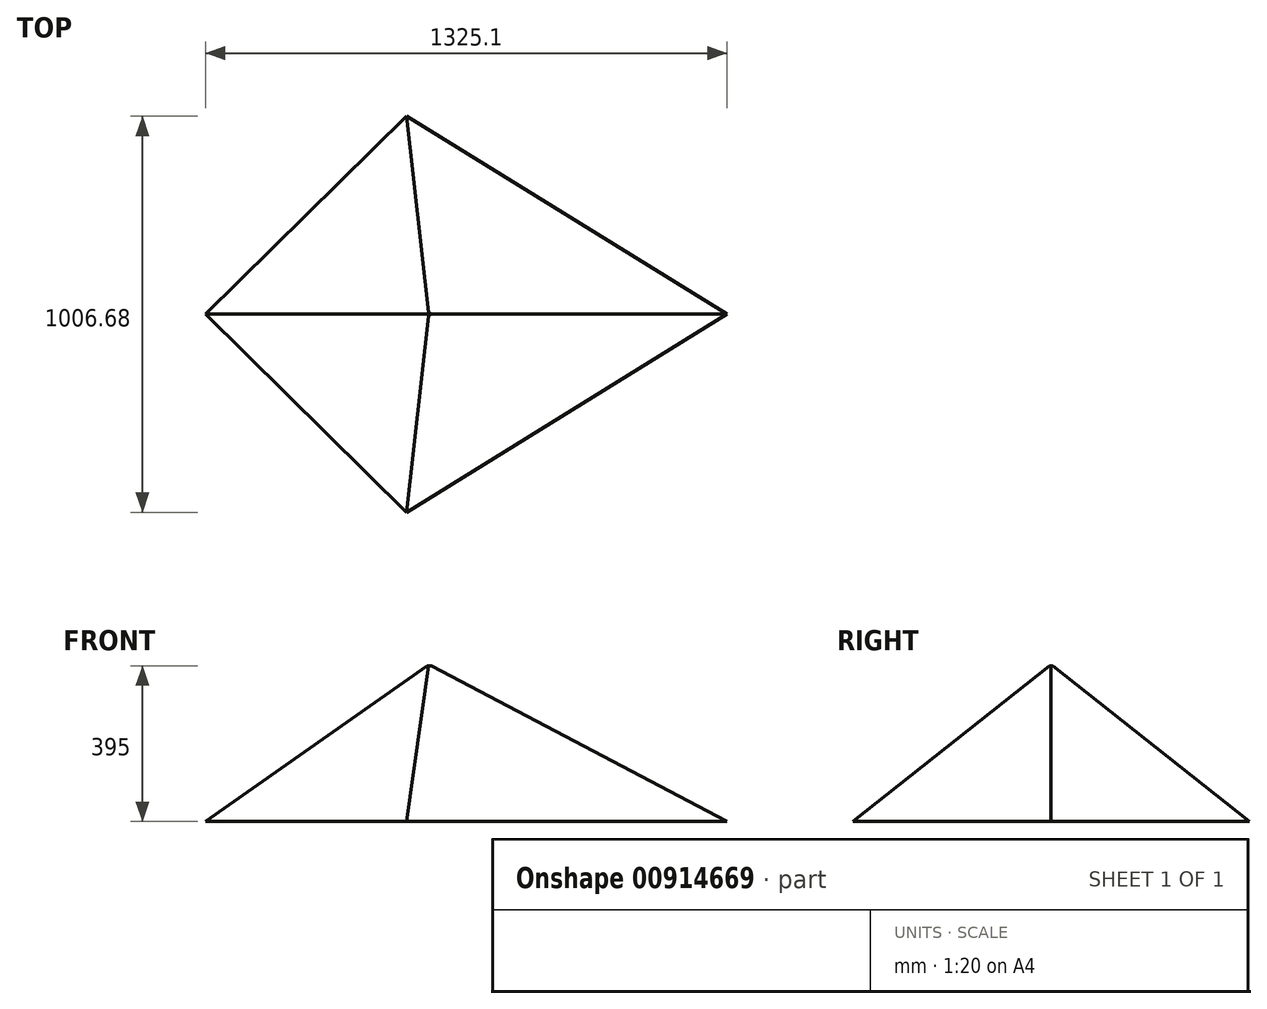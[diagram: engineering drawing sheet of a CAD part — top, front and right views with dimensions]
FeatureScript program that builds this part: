
annotation { "Feature Type Name" : "Feature", "Feature Type Description" : "" }
export const myFeature = defineFeature(function(context is Context, id is Id, definition is map)
    precondition{}
    {
        {
            var Q0;
            Q0=qCreatedBy(makeId("Top.planeOp"),FACE);
            var sketch = newSketch(context, id + "F0", { "sketchPlane" : qUnion([Q0])});
            skLineSegment(sketch, "E0", {"start": v(-534.54, 0) * mm, "end": v(0, -526.09) * mm});
            skLineSegment(sketch, "E1", {"start": v(0, -526.09) * mm, "end": v(850.43, 0) * mm});
            skLineSegment(sketch, "E2", {"start": v(850.43, 0) * mm, "end": v(0, 526.09) * mm});
            skLineSegment(sketch, "E3", {"start": v(0, 526.09) * mm, "end": v(-534.54, 0) * mm});
            skLineSegment(sketch, "E4.0", {"start": v(2.55, 503.34) * mm, "end": v(-508.88, 0) * mm});
            skLineSegment(sketch, "E4.1", {"start": v(816.22, 0) * mm, "end": v(2.55, 503.34) * mm});
            skLineSegment(sketch, "E4.2", {"start": v(2.55, -503.34) * mm, "end": v(816.22, 0) * mm});
            skLineSegment(sketch, "E4.3", {"start": v(-508.88, 0) * mm, "end": v(2.55, -503.34) * mm});
            skSolve(sketch);
        }
        {
            var Q0;
            Q0=makeQuery(id+"F0.imprint","IMPRINT",FACE,{"disambiguationData":[TD([[makeQuery(id+"F0.imprint","IMPRINT",EDGE,{"derivedFrom":sQuery(id+"F0.wireOp",EDGE,"E4.0")}),1.0]])]});
            extrude(context, id + "F1", {"entities" : qUnion([Q0]), "depth" : 395 * mm, "offsetDistance" : 25 * mm});
        }
        {
            var Q0;
            Q0=makeQuery(id+"F1.opExtrude","CAP_EDGE",EDGE,{"disambiguationData":[OSD([sQuery(id+"F0.wireOp",EDGE,"E4.3")])],"isStart":false});
            var Q1;
            Q1=makeQuery(id+"F1.opExtrude","CAP_EDGE",EDGE,{"disambiguationData":[OSD([sQuery(id+"F0.wireOp",EDGE,"E4.2")])],"isStart":false});
            var Q2;
            Q2=makeQuery(id+"F1.opExtrude","CAP_EDGE",EDGE,{"disambiguationData":[OSD([sQuery(id+"F0.wireOp",EDGE,"E4.1")])],"isStart":false});
            var Q3;
            Q3=makeQuery(id+"F1.opExtrude","CAP_EDGE",EDGE,{"disambiguationData":[OSD([sQuery(id+"F0.wireOp",EDGE,"E4.0")])],"isStart":false});
            chamfer(context, id + "F2", {"entities" : qUnion([Q0, Q1, Q2, Q3]), "width" : 395 * mm, "tangentPropagation" : true});
        }
    });
